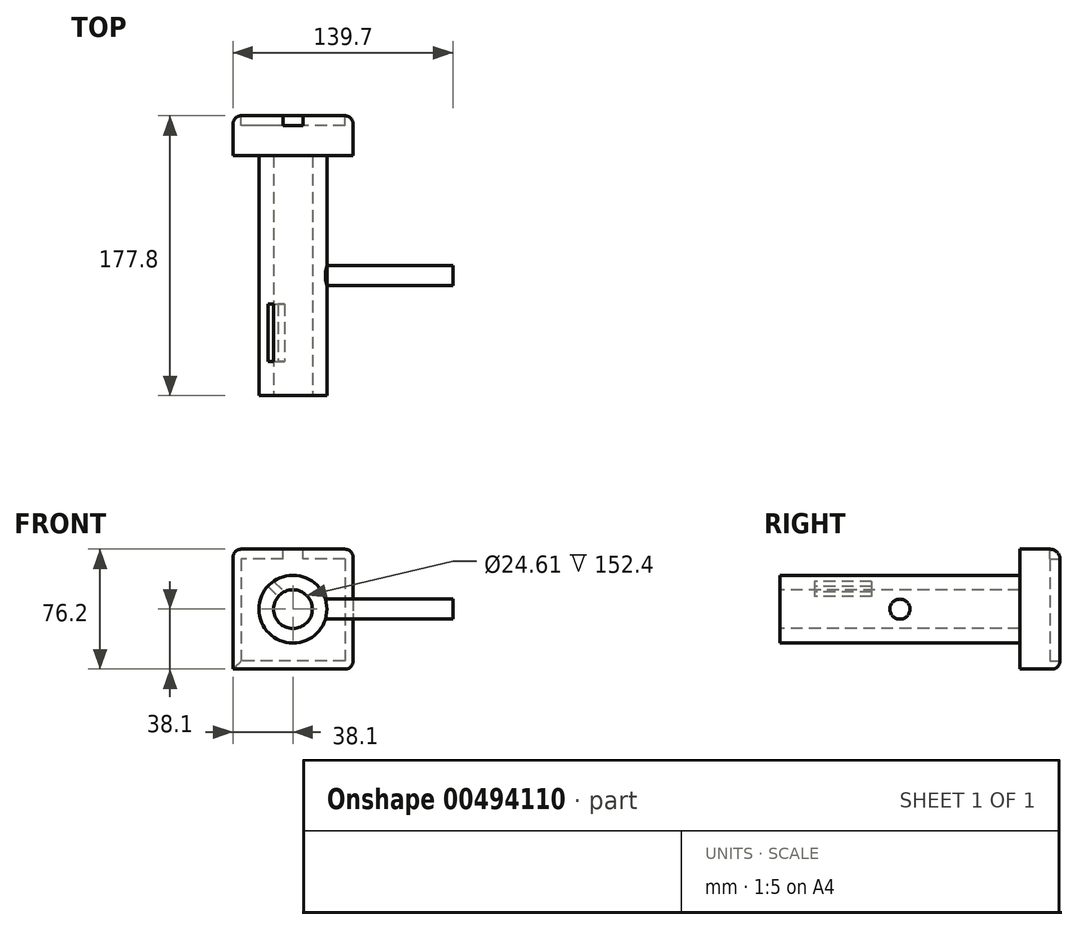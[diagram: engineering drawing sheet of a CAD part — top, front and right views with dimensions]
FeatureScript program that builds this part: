
annotation { "Feature Type Name" : "Feature", "Feature Type Description" : "" }
export const myFeature = defineFeature(function(context is Context, id is Id, definition is map)
    precondition{}
    {
        {
            var Q0;
            Q0=qCreatedBy(makeId("Front.planeOp"),FACE);
            var sketch = newSketch(context, id + "F0", { "sketchPlane" : qUnion([Q0])});
            skCircle(sketch, "E0", {"center": v(0, 0) * mm, "radius": 21.57 * mm});
            skCircle(sketch, "E1", {"center": v(0, 0) * mm, "radius": 12.3 * mm});
            skSolve(sketch);
        }
        {
            var Q0;
            Q0=makeQuery(id+"F0.imprint","IMPRINT",FACE,{"disambiguationData":[TD([[makeQuery(id+"F0.imprint","IMPRINT",EDGE,{"derivedFrom":sQuery(id+"F0.wireOp",EDGE,"E0")}),1.0]])]});
            extrude(context, id + "F1", {"entities" : qUnion([Q0]), "endBound" : BoundingType.SYMMETRIC, "oppositeDirection" : true, "depth" : 152.4 * mm});
        }
        {
            var Q0;
            Q0=qCreatedBy(makeId("Right.planeOp"),FACE);
            var Q1;
            Q1=makeQuery(id+"F1.opExtrude","CAP_EDGE",EDGE,{"disambiguationData":[OSD([sQuery(id+"F0.wireOp",EDGE,"E1")])],"isStart":true});
            cPlane(context, id + "F2", {"entities" : qUnion([Q0, Q1]), "cplaneType" : CPlaneType.LINE_ANGLE, "offset" : 25.4 * mm, "angle" : 45 * degree, "oppositeDirection" : true, "width" : 152.4 * mm, "height" : 152.4 * mm});
        }
        {
            var Q0;
            Q0=qCreatedBy(id+"F2.planeOp",FACE);
            var sketch = newSketch(context, id + "F3", { "sketchPlane" : qUnion([Q0])});
            skLineSegment(sketch, "E2", {"start": v(54.37, 3.9) * mm, "end": v(17.96, 3.9) * mm});
            skLineSegment(sketch, "E3.0", {"start": v(54.37, -0.92) * mm, "end": v(17.96, -0.92) * mm});
            skLineSegment(sketch, "E4", {"start": v(54.37, 3.9) * mm, "end": v(54.37, -0.92) * mm});
            skLineSegment(sketch, "E5", {"start": v(17.96, 3.9) * mm, "end": v(17.96, -0.92) * mm});
            skSolve(sketch);
        }
        {
            var Q0;
            Q0=makeQuery(id+"F3.imprint","IMPRINT",FACE,{"disambiguationData":[TD([[makeQuery(id+"F3.imprint","IMPRINT",EDGE,{"derivedFrom":sQuery(id+"F3.wireOp",EDGE,"E2")}),1.0]])]});
            extrude(context, id + "F4", {"entities" : qUnion([Q0]), "operationType" : NewBodyOperationType.REMOVE, "depth" : 25.4 * mm});
        }
        {
            var Q0;
            Q0=qCreatedBy(makeId("Right.planeOp"),FACE);
            cPlane(context, id + "F5", {"entities" : qUnion([Q0]), "cplaneType" : CPlaneType.OFFSET, "offset" : 101.6 * mm, "width" : 152.4 * mm, "height" : 152.4 * mm});
        }
        {
            var Q0;
            Q0=qCreatedBy(id+"F5.planeOp",FACE);
            var sketch = newSketch(context, id + "F6", { "sketchPlane" : qUnion([Q0])});
            skCircle(sketch, "E6", {"center": v(0, 0) * mm, "radius": 6.35 * mm});
            skSolve(sketch);
        }
        {
            var Q0;
            Q0=makeQuery(id+"F6.imprint","IMPRINT",FACE,{"disambiguationData":[TD([[makeQuery(id+"F6.imprint","IMPRINT",EDGE,{"derivedFrom":sQuery(id+"F6.wireOp",EDGE,"E6")}),1.0]])]});
            var Q1;
            Q1=makeQuery(id+"F1.opExtrude","SWEPT_BODY",BODY,{"disambiguationData":[OSD([sQuery(id+"F0.wireOp",EDGE,"E0"),sQuery(id+"F0.wireOp",EDGE,"E1")])]});
            extrude(context, id + "F7", {"entities" : qUnion([Q0]), "endBound" : BoundingType.UP_TO_BODY, "oppositeDirection" : true, "endBoundEntityBody" : qUnion([Q1]), "depth" : 254 * mm});
        }
        {
            var Q0;
            Q0=makeQuery(id+"F1.opExtrude","CAP_FACE",FACE,{"disambiguationData":[OSD([sQuery(id+"F0.wireOp",EDGE,"E0"),sQuery(id+"F0.wireOp",EDGE,"E1")])],"isStart":false});
            var sketch = newSketch(context, id + "F8", { "sketchPlane" : qUnion([Q0])});
            skCircle(sketch, "E7.0", {"center": v(0, 0) * mm, "radius": 21.57 * mm});
            skSolve(sketch);
        }
        {
            var Q0;
            Q0=makeQuery(id+"F8.imprint","IMPRINT",FACE,{"disambiguationData":[TD([[makeQuery(id+"F8.imprint","IMPRINT",EDGE,{"derivedFrom":sQuery(id+"F8.wireOp",EDGE,"E7.0")}),-1.0]])]});
            var sketch = newSketch(context, id + "F9", { "sketchPlane" : qUnion([Q0])});
            skLineSegment(sketch, "E8.bottom", {"start": v(-38.1, 38.1) * mm, "end": v(38.1, 38.1) * mm});
            skLineSegment(sketch, "E8.top", {"start": v(-38.1, -38.1) * mm, "end": v(38.1, -38.1) * mm});
            skLineSegment(sketch, "E8.left", {"start": v(-38.1, 38.1) * mm, "end": v(-38.1, -38.1) * mm});
            skLineSegment(sketch, "E8.right", {"start": v(38.1, 38.1) * mm, "end": v(38.1, -38.1) * mm});
            skSolve(sketch);
        }
        {
            var Q0;
            Q0=makeQuery(id+"F9.imprint","IMPRINT",FACE,{"disambiguationData":[TD([[makeQuery(id+"F9.imprint","IMPRINT",EDGE,{"derivedFrom":sQuery(id+"F9.wireOp",EDGE,"E8.bottom")}),-1.0]])]});
            var Q1;
            Q1=makeQuery(id+"F8.imprint","IMPRINT",FACE,{"disambiguationData":[TD([[makeQuery(id+"F8.imprint","IMPRINT",EDGE,{"derivedFrom":sQuery(id+"F8.wireOp",EDGE,"E7.0")}),-1.0]])]});
            var Q2;
            Q2=makeQuery(id+"F8.imprint","IMPRINT",FACE,{"disambiguationData":[TD([[makeQuery(id+"F8.imprint","IMPRINT",EDGE,{"derivedFrom":makeQuery(id+"F1.opExtrude","CAP_EDGE",EDGE,{"disambiguationData":[OSD([sQuery(id+"F0.wireOp",EDGE,"E1")])],"isStart":false})}),-1.0]])]});
            extrude(context, id + "F10", {"entities" : qUnion([Q0, Q1, Q2]), "operationType" : NewBodyOperationType.ADD, "depth" : 25.4 * mm});
        }
        {
            var Q0;
            Q0=makeQuery(id+"F10.opExtrude","CAP_EDGE",EDGE,{"disambiguationData":[OSD([sQuery(id+"F9.wireOp",EDGE,"E8.bottom")])],"isStart":false});
            fillet(context, id + "F11", {"entities" : qUnion([Q0]), "radius" : 6.35 * mm, "tangentPropagation" : true, "allowEdgeOverflow" : false});
        }
        {
            var Q0;
            Q0=makeQuery(id+"F10.opExtrude","CAP_EDGE",EDGE,{"disambiguationData":[OSD([sQuery(id+"F9.wireOp",EDGE,"E8.left")])],"isStart":false});
            var Q1;
            Q1=makeQuery(id+"F10.opExtrude","CAP_EDGE",EDGE,{"disambiguationData":[OSD([sQuery(id+"F9.wireOp",EDGE,"E8.top")])],"isStart":false});
            var Q2;
            Q2=makeQuery(id+"F10.opExtrude","CAP_EDGE",EDGE,{"disambiguationData":[OSD([sQuery(id+"F9.wireOp",EDGE,"E8.right")])],"isStart":false});
            fillet(context, id + "F12", {"entities" : qUnion([Q0, Q1, Q2]), "radius" : 5.08 * mm, "tangentPropagation" : true, "allowEdgeOverflow" : false});
        }
        {
            var Q0;
            Q0=makeQuery(id+"F10.opExtrude","SWEPT_EDGE",EDGE,{"disambiguationData":[OSD([sQuery(id+"F9.wireOp",EDGE,"E8.top"),sQuery(id+"F9.wireOp",EDGE,"E8.left")])]});
            fillet(context, id + "F13", {"entities" : qUnion([Q0]), "radius" : 5.08 * mm, "tangentPropagation" : true, "allowEdgeOverflow" : false});
        }
        {
            var Q0;
            {var subQ0=sQuery(id+"F8.wireOp",EDGE,"E7.0");Q0=makeQuery(id+"F10.boolean.opBoolean","MERGE",FACE,{"derivedFrom":[makeQuery(id+"F10.opExtrude","CAP_FACE",FACE,{"disambiguationData":[OSD([subQ0])],"isStart":false}),makeQuery(id+"F10.opExtrude","CAP_FACE",FACE,{"disambiguationData":[OSD([subQ0,sQuery(id+"F9.wireOp",EDGE,"E8.bottom"),sQuery(id+"F9.wireOp",EDGE,"E8.top"),sQuery(id+"F9.wireOp",EDGE,"E8.left"),sQuery(id+"F9.wireOp",EDGE,"E8.right")])],"isStart":false})]});}
            extrude(context, id + "F14", {"entities" : qUnion([Q0]), "operationType" : NewBodyOperationType.REMOVE, "oppositeDirection" : true, "depth" : 6.35 * mm});
        }
        {
            var Q0;
            Q0=makeQuery(id+"F14.boolean.opBoolean","COPY",FACE,{"derivedFrom":makeQuery(id+"F14.opExtrude","CAP_FACE",FACE,{"disambiguationData":[OSD([sQuery(id+"F8.wireOp",EDGE,"E7.0"),sQuery(id+"F9.wireOp",EDGE,"E8.bottom"),sQuery(id+"F9.wireOp",EDGE,"E8.top"),sQuery(id+"F9.wireOp",EDGE,"E8.left"),sQuery(id+"F9.wireOp",EDGE,"E8.right")])],"isStart":false})});
            var sketch = newSketch(context, id + "F15", { "sketchPlane" : qUnion([Q0])});
            skCircle(sketch, "E9", {"center": v(0, 15.4) * mm, "radius": 6.35 * mm});
            skLineSegment(sketch, "E10", {"start": v(-6.35, 15.4) * mm, "end": v(-6.35, 46.86) * mm});
            skLineSegment(sketch, "E11.MirrorCS", {"start": v(6.35, 15.4) * mm, "end": v(6.35, 46.86) * mm});
            skLineSegment(sketch, "E12", {"start": v(-6.35, 46.86) * mm, "end": v(6.35, 46.86) * mm});
            skSolve(sketch);
        }
        {
            var Q0;
            {var subQ0=sQuery(id+"F15.wireOp",EDGE,"E10");var subQ1=sQuery(id+"F15.wireOp",EDGE,"E9");var subQ2=makeQuery(id+"F15.imprint","INTERSECT",VERTEX,{"derivedFrom":[subQ1,subQ0]});Q0=makeQuery(id+"F15.imprint","IMPRINT",FACE,{"disambiguationData":[TD([[makeQuery(id+"F15.imprint","IMPRINT",EDGE,{"disambiguationData":[TD([[subQ2,1.0]])],"derivedFrom":subQ1}),-1.0]])]});}
            var Q1;
            {var subQ0=sQuery(id+"F15.wireOp",EDGE,"E12");Q1=makeQuery(id+"F15.imprint","IMPRINT",FACE,{"disambiguationData":[TD([[makeQuery(id+"F15.imprint","IMPRINT",EDGE,{"derivedFrom":subQ0}),-1.0]])]});}
            var Q2;
            {var subQ0=sQuery(id+"F15.wireOp",EDGE,"E9");var subQ1=makeQuery(id+"F15.imprint","INTERSECT",VERTEX,{"derivedFrom":[subQ0,sQuery(id+"F15.wireOp",EDGE,"E10")]});Q2=makeQuery(id+"F15.imprint","IMPRINT",FACE,{"disambiguationData":[TD([[makeQuery(id+"F15.imprint","IMPRINT",EDGE,{"disambiguationData":[TD([[subQ1,1.0]])],"derivedFrom":subQ0}),1.0]])]});}
            extrude(context, id + "F16", {"entities" : qUnion([Q0, Q1, Q2]), "operationType" : NewBodyOperationType.REMOVE, "depth" : 25.4 * mm, "offsetDistance" : 25.4 * mm});
        }
    });
